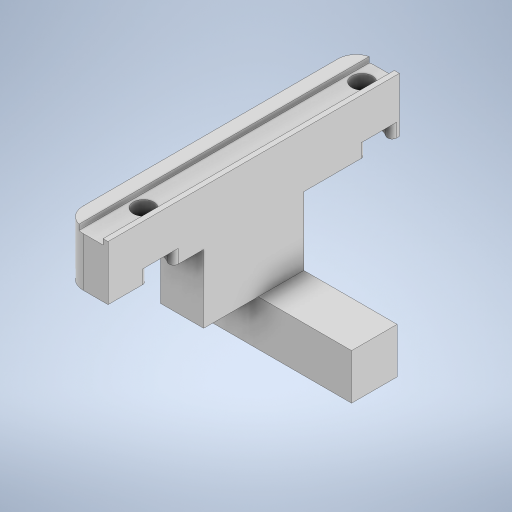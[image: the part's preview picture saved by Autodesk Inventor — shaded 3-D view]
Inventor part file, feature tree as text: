
AUTODESK INVENTOR PART (.ipt)
format: ipt  version: 2024 (Build 280153000, 153)  size: 317,952 bytes
history: native  units: in
note: dims shown in document units (in); Inventor stores cm internally (conversion verified against a paired STEP export)
features: extrude x5, sketch x5, projected_geometry x4, fillet x2
ambient origin geometry x8: Origin, YZ Plane, XZ Plane, XY Plane, X Axis, Y Axis, Z Axis, Center Point
bodies: Solid1 (feature_tree)
feature tree (16):
  extrude  "Extrusion1"  Depth=2.5197in
  extrude  "Extrusion2"  Depth=1.8898in
  extrude  "Extrusion3"  Depth=0.4724in TaperAngle=0.0deg
  fillet  "Fillet1"  Radius=0.0433in
  fillet  "Fillet2"  Radius=0.2126in
  extrude  "Extrusion15"  Depth=0.4724in TaperAngle=0.0deg
  extrude  "Extrusion17"  Depth=0.1181in TaperAngle=0.0deg
  sketch  "Sketch1"  dims[d1=0.374in d2=2.5197in]
  sketch  "Sketch2"  dims[d3=0.1772in d4=1.8898in]
  sketch  "Sketch3"  dims[d6=0.1457in d7=0.4724in d8=0.0in d9=0.0433in d10=0.2126in]
  projected_geometry  "Projected Loop2"
  projected_geometry  "Projected Loop3"
  projected_geometry  "Projected Loop4"
  projected_geometry  "Projected Loop5"
  sketch  "Sketch15"  dims[d11=0.0472in d12=0.4724in d13=0.0in]
  sketch  "Sketch21"  dims[d14=0.2953in d15=0.1181in d16=0.0in d17=0.1772in d18=0.0394in d19=0.1575in d76=0.4724in d79=0.4331in d80=0.8661in d81=0.5906in d82=0.0in d93=0.3937in d94=0.3937in d95=1.5748in d96=0.3937in d97=0.3937in d98=0.0in d42=0.0197in d43=0.0344in d44=0.0197in d45=0.0344in d46=0.0in d47=0.0in d48=0.0in d49=0.0in d50=0.0in d51=0.0in d52=0.0in d53=0.0in d55=0.0197in d56=0.0344in d57=0.0197in d58=0.0344in d60=0.0197in d61=0.0344in d62=0.0197in d63=0.0344in d72=0.0197in d73=0.0344in d74=0.0197in d75=0.0344in]
